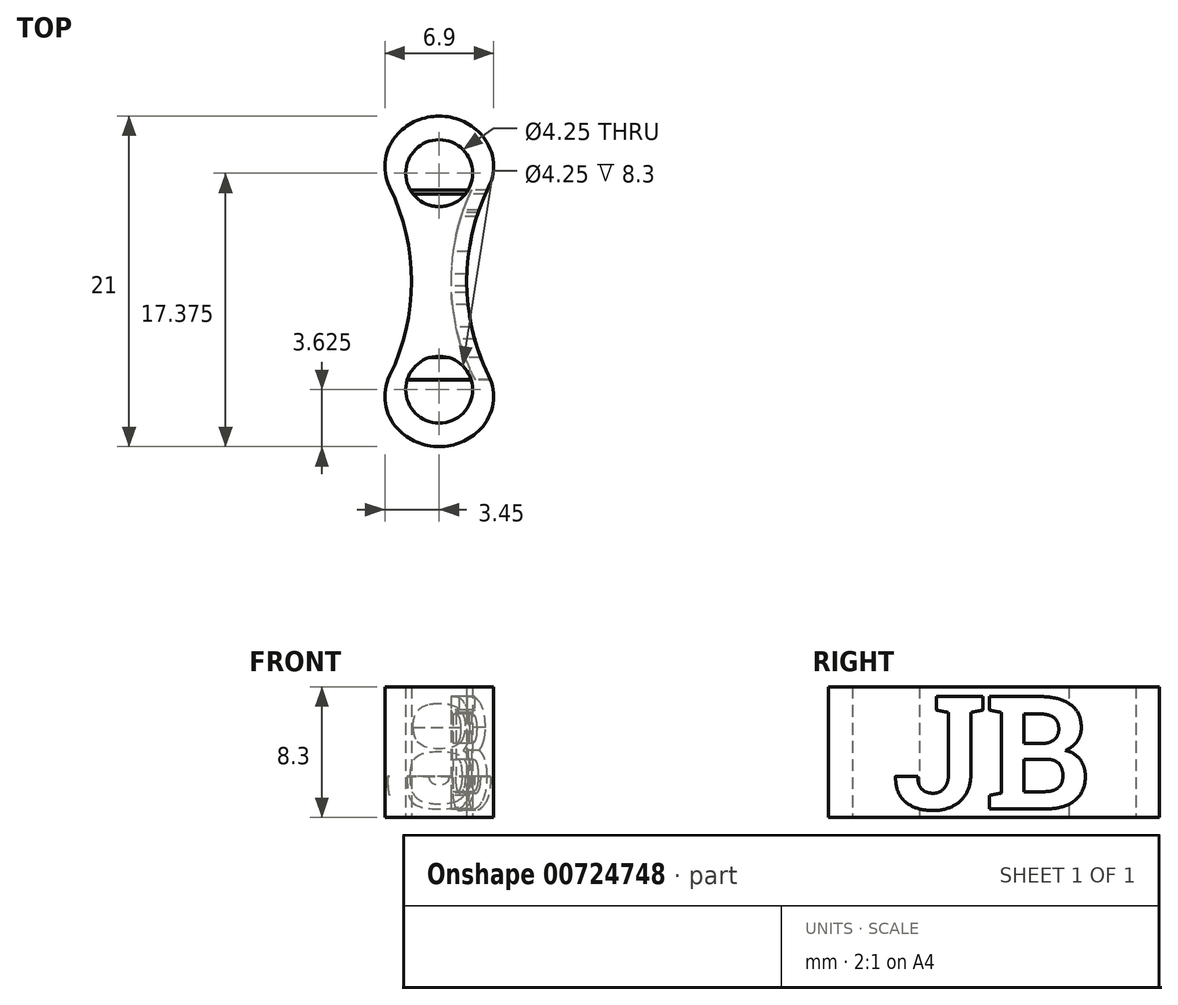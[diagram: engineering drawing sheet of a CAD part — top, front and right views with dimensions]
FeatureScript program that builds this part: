
annotation { "Feature Type Name" : "Feature", "Feature Type Description" : "" }
export const myFeature = defineFeature(function(context is Context, id is Id, definition is map)
    precondition{}
    {
        {
            var Q0;
            Q0=qCreatedBy(makeId("Top.planeOp"),FACE);
            var sketch = newSketch(context, id + "F0", { "sketchPlane" : qUnion([Q0])});
            skLineSegment(sketch, "E0", {"start": v(0, 6.88) * mm, "end": v(0, -6.88) * mm});
            skCircle(sketch, "E1", {"center": v(0, 6.88) * mm, "radius": 2.12 * mm});
            skLineSegment(sketch, "E2", {"start": v(-1.75, 0) * mm, "end": v(1.75, 0) * mm});
            skCircle(sketch, "E3", {"center": v(0, -6.88) * mm, "radius": 2.12 * mm});
            skCircle(sketch, "E4", {"center": v(0, 6.88) * mm, "radius": 3.62 * mm});
            skCircle(sketch, "E5", {"center": v(0, -6.88) * mm, "radius": 3.62 * mm});
            skArc(sketch, "E6", {"start": v(-3.12, -5.03) * mm, "mid": v(-1.75, 0) * mm, "end": v(-3.12, 5.03) * mm});
            skArc(sketch, "E7.MirrorCS", {"start": v(3.12, -5.03) * mm, "mid": v(1.75, 0) * mm, "end": v(3.12, 5.03) * mm});
            skPoint(sketch, "E8.orphan", {"position": v(3.12, 5.03) * mm});
            skPoint(sketch, "E9.orphan", {"position": v(-3.12, 5.03) * mm});
            skPoint(sketch, "E10.orphan", {"position": v(6.24, 6.88) * mm});
            skArc(sketch, "E11", {"start": v(-3.63, -6.87) * mm, "mid": v(-1.75, 0) * mm, "end": v(-3.63, 6.87) * mm});
            skArc(sketch, "E12.MirrorCS", {"start": v(3.63, -6.87) * mm, "mid": v(1.75, 0) * mm, "end": v(3.63, 6.87) * mm});
            skSolve(sketch);
        }
        {
            var Q0;
            Q0=makeQuery(id+"F0.imprint","IMPRINT",FACE,{"disambiguationData":[TD([[makeQuery(id+"F0.imprint","IMPRINT",EDGE,{"derivedFrom":sQuery(id+"F0.wireOp",EDGE,"E1")}),-1.0]])]});
            var Q1;
            {var subQ0=sQuery(id+"F0.wireOp",EDGE,"E4");var subQ1=sQuery(id+"F0.wireOp",EDGE,"E0");var subQ2=makeQuery(id+"F0.imprint","INTERSECT",VERTEX,{"derivedFrom":[subQ1,subQ0]});Q1=makeQuery(id+"F0.imprint","IMPRINT",FACE,{"disambiguationData":[TD([[makeQuery(id+"F0.imprint","IMPRINT",EDGE,{"disambiguationData":[TD([[subQ2,-1.0]])],"derivedFrom":subQ1}),-1.0]])]});}
            var Q2;
            {var subQ0=sQuery(id+"F0.wireOp",EDGE,"E4");var subQ1=sQuery(id+"F0.wireOp",EDGE,"E0");var subQ2=makeQuery(id+"F0.imprint","INTERSECT",VERTEX,{"derivedFrom":[subQ1,subQ0]});Q2=makeQuery(id+"F0.imprint","IMPRINT",FACE,{"disambiguationData":[TD([[makeQuery(id+"F0.imprint","IMPRINT",EDGE,{"disambiguationData":[TD([[subQ2,-1.0]])],"derivedFrom":subQ1}),1.0]])]});}
            var Q3;
            {var subQ0=sQuery(id+"F0.wireOp",EDGE,"E5");var subQ1=sQuery(id+"F0.wireOp",EDGE,"E0");var subQ2=makeQuery(id+"F0.imprint","INTERSECT",VERTEX,{"derivedFrom":[subQ1,subQ0]});Q3=makeQuery(id+"F0.imprint","IMPRINT",FACE,{"disambiguationData":[TD([[makeQuery(id+"F0.imprint","IMPRINT",EDGE,{"disambiguationData":[TD([[subQ2,1.0]])],"derivedFrom":subQ1}),1.0]])]});}
            var Q4;
            {var subQ0=sQuery(id+"F0.wireOp",EDGE,"E5");var subQ1=sQuery(id+"F0.wireOp",EDGE,"E0");var subQ2=makeQuery(id+"F0.imprint","INTERSECT",VERTEX,{"derivedFrom":[subQ1,subQ0]});Q4=makeQuery(id+"F0.imprint","IMPRINT",FACE,{"disambiguationData":[TD([[makeQuery(id+"F0.imprint","IMPRINT",EDGE,{"disambiguationData":[TD([[subQ2,1.0]])],"derivedFrom":subQ1}),-1.0]])]});}
            var Q5;
            Q5=makeQuery(id+"F0.imprint","IMPRINT",FACE,{"disambiguationData":[TD([[makeQuery(id+"F0.imprint","IMPRINT",EDGE,{"derivedFrom":sQuery(id+"F0.wireOp",EDGE,"E3")}),-1.0]])]});
            extrude(context, id + "F1", {"entities" : qUnion([Q0, Q1, Q2, Q3, Q4, Q5]), "depth" : 8.3 * mm, "offsetDistance" : 25 * mm});
        }
        {
            var Q0;
            Q0=makeQuery(id+"F1.opExtrude","CAP_VERTEX",VERTEX,{"disambiguationData":[OSD([sQuery(id+"F0.wireOp",EDGE,"E4"),sQuery(id+"F0.wireOp",EDGE,"E11")])],"isStart":false});
            var Q1;
            Q1=makeQuery(id+"F1.opExtrude","CAP_VERTEX",VERTEX,{"disambiguationData":[OSD([sQuery(id+"F0.wireOp",EDGE,"E4"),sQuery(id+"F0.wireOp",EDGE,"E11")])],"isStart":true});
            var Q2;
            Q2=makeQuery(id+"F1.opExtrude","CAP_VERTEX",VERTEX,{"disambiguationData":[OSD([sQuery(id+"F0.wireOp",EDGE,"E5"),sQuery(id+"F0.wireOp",EDGE,"E11")])],"isStart":true});
            cPlane(context, id + "F2", {"entities" : qUnion([Q0, Q1, Q2]), "cplaneType" : CPlaneType.THREE_POINT, "offset" : 10 * mm, "width" : 150 * mm, "height" : 150 * mm});
        }
        {
            var Q0;
            Q0=qCreatedBy(id+"F2.planeOp",FACE);
            var sketch = newSketch(context, id + "F3", { "sketchPlane" : qUnion([Q0])});
            skLineSegment(sketch, "E13", {"start": v(-1.85, 4.15) * mm, "end": v(1.85, 4.15) * mm});
            skPoint(sketch, "E14", {"position": v(0, 4.15) * mm});
            skSolve(sketch);
        }
        {
            var Q0;
            Q0=qCreatedBy(id+"F2.planeOp",FACE);
            var sketch = newSketch(context, id + "F4", { "sketchPlane" : qUnion([Q0])});
            skText(sketch, "E15", { "text": "JB", "fontName": "RobotoSlab-Bold.ttf"});
            const initialGuessF4  = {"E15": [-0.00642, 0.00054, 1, 0, 0.00723]};
            skSetInitialGuess(sketch, initialGuessF4);
            skSolve(sketch);
        }
        {
            var Q0;
            Q0=makeQuery(id+"F4.imprint","IMPRINT",FACE,{"disambiguationData":[TD([[makeQuery(id+"F4.imprint","IMPRINT",EDGE,{"derivedFrom":sQuery(id+"F4.wireOp",EDGE,"E15.sketch_text.stroke-18")}),-1.0]])]});
            var Q1;
            Q1=makeQuery(id+"F4.imprint","IMPRINT",FACE,{"disambiguationData":[TD([[makeQuery(id+"F4.imprint","IMPRINT",EDGE,{"derivedFrom":sQuery(id+"F4.wireOp",EDGE,"E15.sketch_text.stroke-0")}),-1.0]])]});
            var Q2;
            Q2=makeQuery(id+"F1.opExtrude","SWEPT_FACE",FACE,{"disambiguationData":[OSD([sQuery(id+"F0.wireOp",EDGE,"E12.MirrorCS")])]});
            extrude(context, id + "F5", {"entities" : qUnion([Q0, Q1]), "operationType" : NewBodyOperationType.REMOVE, "endBound" : BoundingType.UP_TO_SURFACE, "depth" : 25 * mm, "endBoundEntityFace" : qUnion([Q2]), "hasOffset" : true, "offsetDistance" : 1 * mm, "offsetOppositeDirection" : true});
        }
        {
            var Q0;
            Q0=makeQuery(id+"F1.opExtrude","SWEPT_EDGE",EDGE,{"disambiguationData":[OSD([sQuery(id+"F0.wireOp",EDGE,"E4"),sQuery(id+"F0.wireOp",EDGE,"E11")])]});
            var Q1;
            Q1=makeQuery(id+"F1.opExtrude","SWEPT_EDGE",EDGE,{"disambiguationData":[OSD([sQuery(id+"F0.wireOp",EDGE,"E5"),sQuery(id+"F0.wireOp",EDGE,"E11")])]});
            var Q2;
            Q2=makeQuery(id+"F1.opExtrude","SWEPT_EDGE",EDGE,{"disambiguationData":[OSD([sQuery(id+"F0.wireOp",EDGE,"E5"),sQuery(id+"F0.wireOp",EDGE,"E12.MirrorCS")])]});
            var Q3;
            Q3=makeQuery(id+"F1.opExtrude","SWEPT_EDGE",EDGE,{"disambiguationData":[OSD([sQuery(id+"F0.wireOp",EDGE,"E4"),sQuery(id+"F0.wireOp",EDGE,"E12.MirrorCS")])]});
            fillet(context, id + "F6", {"entities" : qUnion([Q0, Q1, Q2, Q3]), "radius" : 3 * mm, "tangentPropagation" : true, "allowEdgeOverflow" : false});
        }
        {
            var Q0;
            Q0=makeQuery(id+"F4.imprint","IMPRINT",FACE,{"disambiguationData":[TD([[makeQuery(id+"F4.imprint","IMPRINT",EDGE,{"derivedFrom":sQuery(id+"F4.wireOp",EDGE,"E15.sketch_text.stroke-18")}),-1.0]])]});
            var Q1;
            Q1=makeQuery(id+"F4.imprint","IMPRINT",FACE,{"disambiguationData":[TD([[makeQuery(id+"F4.imprint","IMPRINT",EDGE,{"derivedFrom":sQuery(id+"F4.wireOp",EDGE,"E15.sketch_text.stroke-0")}),-1.0]])]});
            var Q2;
            {var subQ0=sQuery(id+"F0.wireOp",EDGE,"E12.MirrorCS");var subQ3=sQuery(id+"F0.wireOp",EDGE,"E4");Q2=makeQuery(id+"F5.boolean.opBoolean","SPLIT",FACE,{"disambiguationData":[TD([makeQuery(id+"F1.opExtrude","SWEPT_FACE",FACE,{"disambiguationData":[OSD([subQ3])]})])],"derivedFrom":makeQuery(id+"F1.opExtrude","SWEPT_FACE",FACE,{"disambiguationData":[OSD([subQ0])]})});}
            var Q3;
            {var subQ1=sQuery(id+"F0.wireOp",EDGE,"E11");var subQ3=sQuery(id+"F0.wireOp",EDGE,"E4");Q3=makeQuery(id+"F5.boolean.opBoolean","SPLIT",FACE,{"disambiguationData":[TD([makeQuery(id+"F1.opExtrude","SWEPT_FACE",FACE,{"disambiguationData":[OSD([subQ3])]})])],"derivedFrom":makeQuery(id+"F1.opExtrude","SWEPT_FACE",FACE,{"disambiguationData":[OSD([subQ1])]})});}
            extrude(context, id + "F7", {"entities" : qUnion([Q0, Q1]), "operationType" : NewBodyOperationType.ADD, "endBound" : BoundingType.UP_TO_SURFACE, "depth" : 25 * mm, "endBoundEntityFace" : qUnion([Q2]), "hasOffset" : true, "offsetDistance" : 1 * mm, "hasSecondDirection" : true, "secondDirectionBound" : SecondDirectionBoundingType.UP_TO_SURFACE, "secondDirectionOppositeDirection" : false, "secondDirectionDepth" : 25 * mm, "secondDirectionBoundEntityFace" : qUnion([Q3])});
        }
    });
